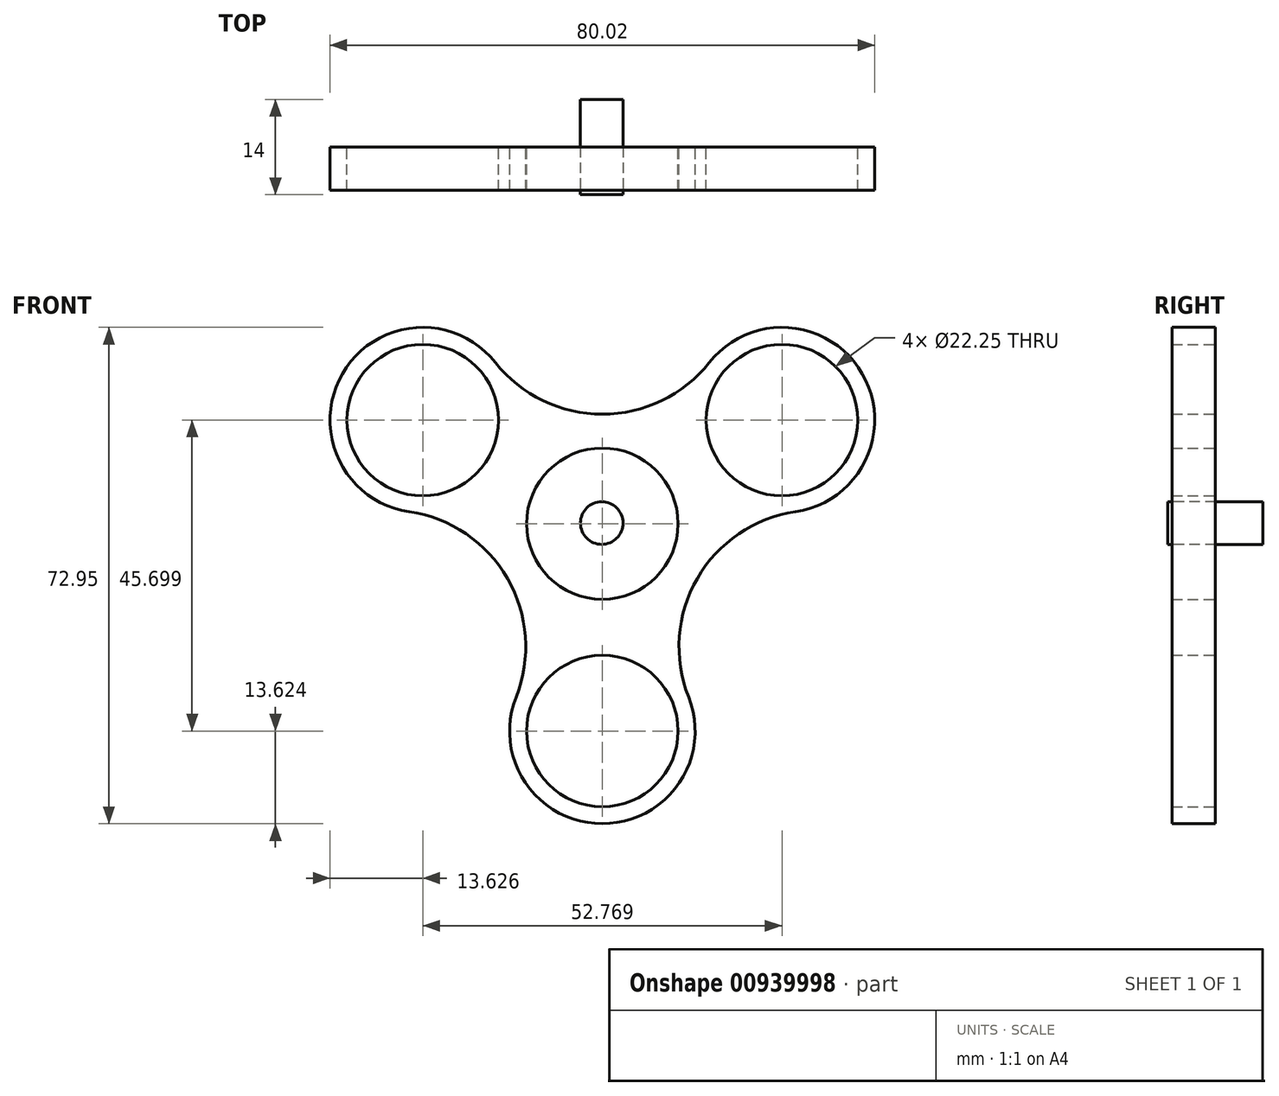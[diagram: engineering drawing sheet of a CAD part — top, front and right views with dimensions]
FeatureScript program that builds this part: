
annotation { "Feature Type Name" : "Feature", "Feature Type Description" : "" }
export const myFeature = defineFeature(function(context is Context, id is Id, definition is map)
    precondition{}
    {
        {
            var Q0;
            Q0=qCreatedBy(makeId("Front.planeOp"),FACE);
            var sketch = newSketch(context, id + "F0", { "sketchPlane" : qUnion([Q0])});
            skCircle(sketch, "E0", {"center": v(0, 0) * mm, "radius": 11.12 * mm});
            skCircle(sketch, "E1", {"center": v(0, -30.47) * mm, "radius": 11.12 * mm});
            skCircle(sketch, "E2.1.0", {"center": v(26.38, 15.23) * mm, "radius": 11.12 * mm});
            skCircle(sketch, "E2.2.0", {"center": v(-26.38, 15.23) * mm, "radius": 11.12 * mm});
            skCircle(sketch, "E3.0", {"center": v(26.38, 15.23) * mm, "radius": 13.62 * mm});
            skCircle(sketch, "E4.0", {"center": v(0, -30.47) * mm, "radius": 13.62 * mm});
            skCircle(sketch, "E5.0", {"center": v(-26.38, 15.23) * mm, "radius": 13.62 * mm});
            skCircle(sketch, "E6", {"center": v(-31.28, -18.06) * mm, "radius": 20.03 * mm});
            skCircle(sketch, "E7.1.0", {"center": v(31.28, -18.06) * mm, "radius": 20.03 * mm});
            skCircle(sketch, "E7.2.0", {"center": v(0, 36.12) * mm, "radius": 20.03 * mm});
            skSolve(sketch);
        }
        {
            var Q0;
            Q0=makeQuery(id+"F0.imprint","IMPRINT",FACE,{"disambiguationData":[TD([[makeQuery(id+"F0.imprint","IMPRINT",EDGE,{"derivedFrom":sQuery(id+"F0.wireOp",EDGE,"E0")}),-1.0]])]});
            var Q1;
            Q1=makeQuery(id+"F0.imprint","IMPRINT",FACE,{"disambiguationData":[TD([[makeQuery(id+"F0.imprint","IMPRINT",EDGE,{"derivedFrom":sQuery(id+"F0.wireOp",EDGE,"E2.1.0")}),-1.0]])]});
            var Q2;
            Q2=makeQuery(id+"F0.imprint","IMPRINT",FACE,{"disambiguationData":[TD([[makeQuery(id+"F0.imprint","IMPRINT",EDGE,{"derivedFrom":sQuery(id+"F0.wireOp",EDGE,"E2.2.0")}),-1.0]])]});
            var Q3;
            Q3=makeQuery(id+"F0.imprint","IMPRINT",FACE,{"disambiguationData":[TD([[makeQuery(id+"F0.imprint","IMPRINT",EDGE,{"derivedFrom":sQuery(id+"F0.wireOp",EDGE,"E1")}),-1.0]])]});
            extrude(context, id + "F1", {"entities" : qUnion([Q0, Q1, Q2, Q3]), "depth" : 6.35 * mm, "offsetDistance" : 25.4 * mm});
        }
        {
            var Q0;
            Q0=qCreatedBy(makeId("Front.planeOp"),FACE);
            var sketch = newSketch(context, id + "F2", { "sketchPlane" : qUnion([Q0])});
            skCircle(sketch, "E8", {"center": v(-0.1, 0.1) * mm, "radius": 3.13 * mm});
            skSolve(sketch);
        }
        {
            var Q0;
            Q0=makeQuery(id+"F2.imprint","IMPRINT",FACE,{"disambiguationData":[TD([[makeQuery(id+"F2.imprint","IMPRINT",EDGE,{"derivedFrom":sQuery(id+"F2.wireOp",EDGE,"E8")}),1.0]])]});
            var Q1;
            Q1=sQuery(id+"F2.wireOp",EDGE,"E8");
            extrude(context, id + "F3", {"entities" : qUnion([Q0]), "surfaceEntities" : qUnion([Q1]), "oppositeDirection" : true, "depth" : 7 * mm, "offsetDistance" : 25.4 * mm, "hasSecondDirection" : true, "secondDirectionOppositeDirection" : false, "secondDirectionDepth" : 7 * mm});
        }
    });
